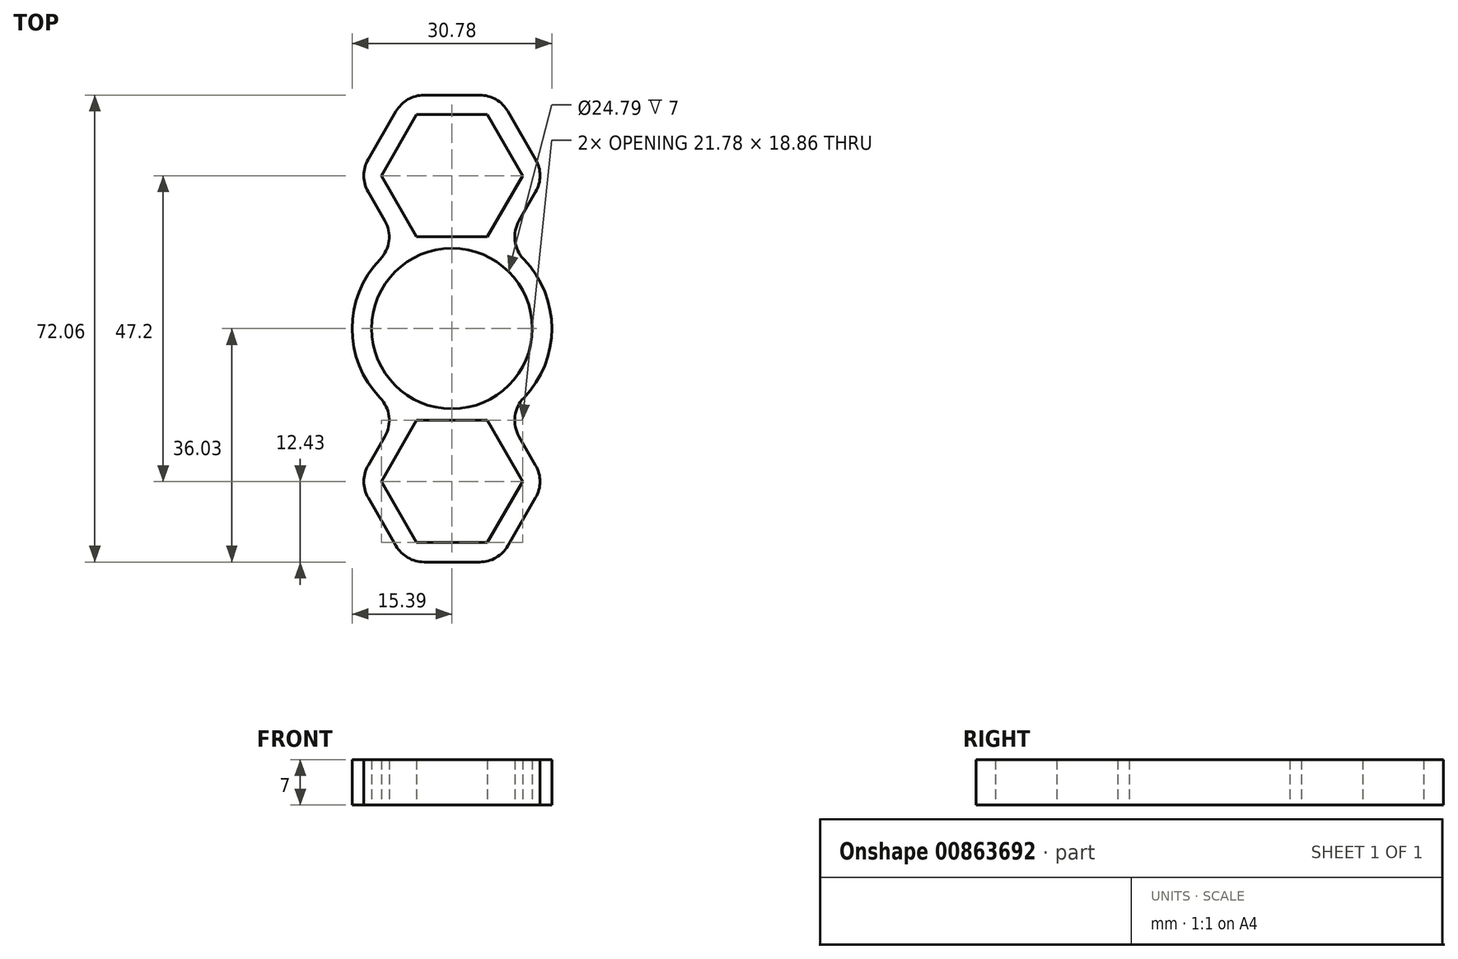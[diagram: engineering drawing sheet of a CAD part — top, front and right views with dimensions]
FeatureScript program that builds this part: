
annotation { "Feature Type Name" : "Feature", "Feature Type Description" : "" }
export const myFeature = defineFeature(function(context is Context, id is Id, definition is map)
    precondition{}
    {
        {
            var Q0;
            Q0=qCreatedBy(makeId("Top.planeOp"),FACE);
            var sketch = newSketch(context, id + "F0", { "sketchPlane" : qUnion([Q0])});
            skCircle(sketch, "E0", {"center": v(0, 0) * mm, "radius": 12.4 * mm});
            skLineSegment(sketch, "E1.0", {"start": v(-5.44, 33.03) * mm, "end": v(5.44, 33.03) * mm});
            skLineSegment(sketch, "E1.1", {"start": v(5.44, 33.03) * mm, "end": v(10.89, 23.6) * mm});
            skLineSegment(sketch, "E1.2", {"start": v(10.89, 23.6) * mm, "end": v(5.44, 14.17) * mm});
            skLineSegment(sketch, "E1.3", {"start": v(5.44, 14.17) * mm, "end": v(-5.44, 14.17) * mm});
            skLineSegment(sketch, "E1.4", {"start": v(-5.44, 14.17) * mm, "end": v(-10.89, 23.6) * mm});
            skLineSegment(sketch, "E1.5", {"start": v(-10.89, 23.6) * mm, "end": v(-5.44, 33.03) * mm});
            skPoint(sketch, "E1.0.midPoint", {"position": v(0, 33.03) * mm});
            skLineSegment(sketch, "E2.0", {"start": v(-4.29, 36.03) * mm, "end": v(4.29, 36.03) * mm});
            skLineSegment(sketch, "E2.1", {"start": v(8.62, 33.53) * mm, "end": v(12.9, 26.1) * mm});
            skLineSegment(sketch, "E2.2", {"start": v(12.9, 21.1) * mm, "end": v(10.35, 16.66) * mm});
            skLineSegment(sketch, "E2.4", {"start": v(-10.35, 16.66) * mm, "end": v(-12.9, 21.1) * mm});
            skLineSegment(sketch, "E2.5", {"start": v(-12.9, 26.1) * mm, "end": v(-8.62, 33.53) * mm});
            skPoint(sketch, "E2.0.midPoint", {"position": v(0, 36.03) * mm});
            skLineSegment(sketch, "E3.MirrorCS", {"start": v(-5.44, -33.03) * mm, "end": v(5.44, -33.03) * mm});
            skLineSegment(sketch, "E4.MirrorCS", {"start": v(-10.35, -16.66) * mm, "end": v(-12.9, -21.1) * mm});
            skPoint(sketch, "E5.MirrorP", {"position": v(0, -36.03) * mm});
            skLineSegment(sketch, "E6.MirrorCS", {"start": v(-4.29, -36.03) * mm, "end": v(4.29, -36.03) * mm});
            skLineSegment(sketch, "E7.MirrorCS", {"start": v(8.62, -33.53) * mm, "end": v(12.9, -26.1) * mm});
            skLineSegment(sketch, "E8.MirrorCS", {"start": v(-10.89, -23.6) * mm, "end": v(-5.44, -33.03) * mm});
            skLineSegment(sketch, "E9.MirrorCS", {"start": v(10.89, -23.6) * mm, "end": v(5.44, -14.17) * mm});
            skLineSegment(sketch, "E10.MirrorCS", {"start": v(12.9, -21.1) * mm, "end": v(10.35, -16.66) * mm});
            skLineSegment(sketch, "E11.MirrorCS", {"start": v(5.44, -14.17) * mm, "end": v(-5.44, -14.17) * mm});
            skPoint(sketch, "E12.MirrorP", {"position": v(0, -33.03) * mm});
            skLineSegment(sketch, "E13.MirrorCS", {"start": v(-12.9, -26.1) * mm, "end": v(-8.62, -33.53) * mm});
            skLineSegment(sketch, "E14.MirrorCS", {"start": v(-5.44, -14.17) * mm, "end": v(-10.89, -23.6) * mm});
            skLineSegment(sketch, "E15.MirrorCS", {"start": v(5.44, -33.03) * mm, "end": v(10.89, -23.6) * mm});
            skArc(sketch, "E16.0", {"start": v(-11.08, 10.69) * mm, "mid": v(-15.4, 0) * mm, "end": v(-11.08, -10.69) * mm});
            skArc(sketch, "E17.trimOffspring", {"start": v(11.08, -10.69) * mm, "mid": v(15.4, 0) * mm, "end": v(11.08, 10.69) * mm});
            skPoint(sketch, "E18.newPointA", {"position": v(-7.18, 11.17) * mm});
            skArc(sketch, "E18.filletArc", {"start": v(-11.08, 10.69) * mm, "mid": v(-9.71, 13.55) * mm, "end": v(-10.35, 16.66) * mm});
            skPoint(sketch, "E19.newPointA", {"position": v(7.18, 11.17) * mm});
            skArc(sketch, "E19.filletArc", {"start": v(10.35, 16.66) * mm, "mid": v(9.71, 13.55) * mm, "end": v(11.08, 10.69) * mm});
            skPoint(sketch, "E20.newPointB", {"position": v(7.18, -11.17) * mm});
            skArc(sketch, "E20.filletArc", {"start": v(11.08, -10.69) * mm, "mid": v(9.71, -13.55) * mm, "end": v(10.35, -16.66) * mm});
            skPoint(sketch, "E21.newPointB", {"position": v(-7.18, -11.17) * mm});
            skArc(sketch, "E21.filletArc", {"start": v(-10.35, -16.66) * mm, "mid": v(-9.71, -13.55) * mm, "end": v(-11.08, -10.69) * mm});
            skPoint(sketch, "E22.visualSharp", {"position": v(14.35, 23.6) * mm});
            skArc(sketch, "E22.filletArc", {"start": v(12.9, 21.1) * mm, "mid": v(13.58, 23.6) * mm, "end": v(12.9, 26.1) * mm});
            skPoint(sketch, "E23.visualSharp", {"position": v(-14.35, 23.6) * mm});
            skArc(sketch, "E23.filletArc", {"start": v(-12.9, 26.1) * mm, "mid": v(-13.58, 23.6) * mm, "end": v(-12.9, 21.1) * mm});
            skPoint(sketch, "E24.visualSharp", {"position": v(-7.18, 36.03) * mm});
            skArc(sketch, "E24.filletArc", {"start": v(-4.29, 36.03) * mm, "mid": v(-6.79, 35.36) * mm, "end": v(-8.62, 33.53) * mm});
            skPoint(sketch, "E25.visualSharp", {"position": v(7.18, 36.03) * mm});
            skArc(sketch, "E25.filletArc", {"start": v(8.62, 33.53) * mm, "mid": v(6.79, 35.36) * mm, "end": v(4.29, 36.03) * mm});
            skPoint(sketch, "E26.visualSharp", {"position": v(14.35, -23.6) * mm});
            skArc(sketch, "E26.filletArc", {"start": v(12.9, -26.1) * mm, "mid": v(13.58, -23.6) * mm, "end": v(12.9, -21.1) * mm});
            skPoint(sketch, "E27.visualSharp", {"position": v(7.18, -36.03) * mm});
            skArc(sketch, "E27.filletArc", {"start": v(4.29, -36.03) * mm, "mid": v(6.79, -35.36) * mm, "end": v(8.62, -33.53) * mm});
            skPoint(sketch, "E28.visualSharp", {"position": v(-7.18, -36.03) * mm});
            skArc(sketch, "E28.filletArc", {"start": v(-8.62, -33.53) * mm, "mid": v(-6.79, -35.36) * mm, "end": v(-4.29, -36.03) * mm});
            skPoint(sketch, "E29.visualSharp", {"position": v(-14.35, -23.6) * mm});
            skArc(sketch, "E29.filletArc", {"start": v(-12.9, -21.1) * mm, "mid": v(-13.58, -23.6) * mm, "end": v(-12.9, -26.1) * mm});
            skSolve(sketch);
        }
        {
            var Q0;
            Q0 = qSketchRegion(id + "F0", true);
            extrude(context, id + "F1", {"entities" : qUnion([Q0]), "depth" : 7 * mm, "offsetDistance" : 25 * mm});
        }
    });
